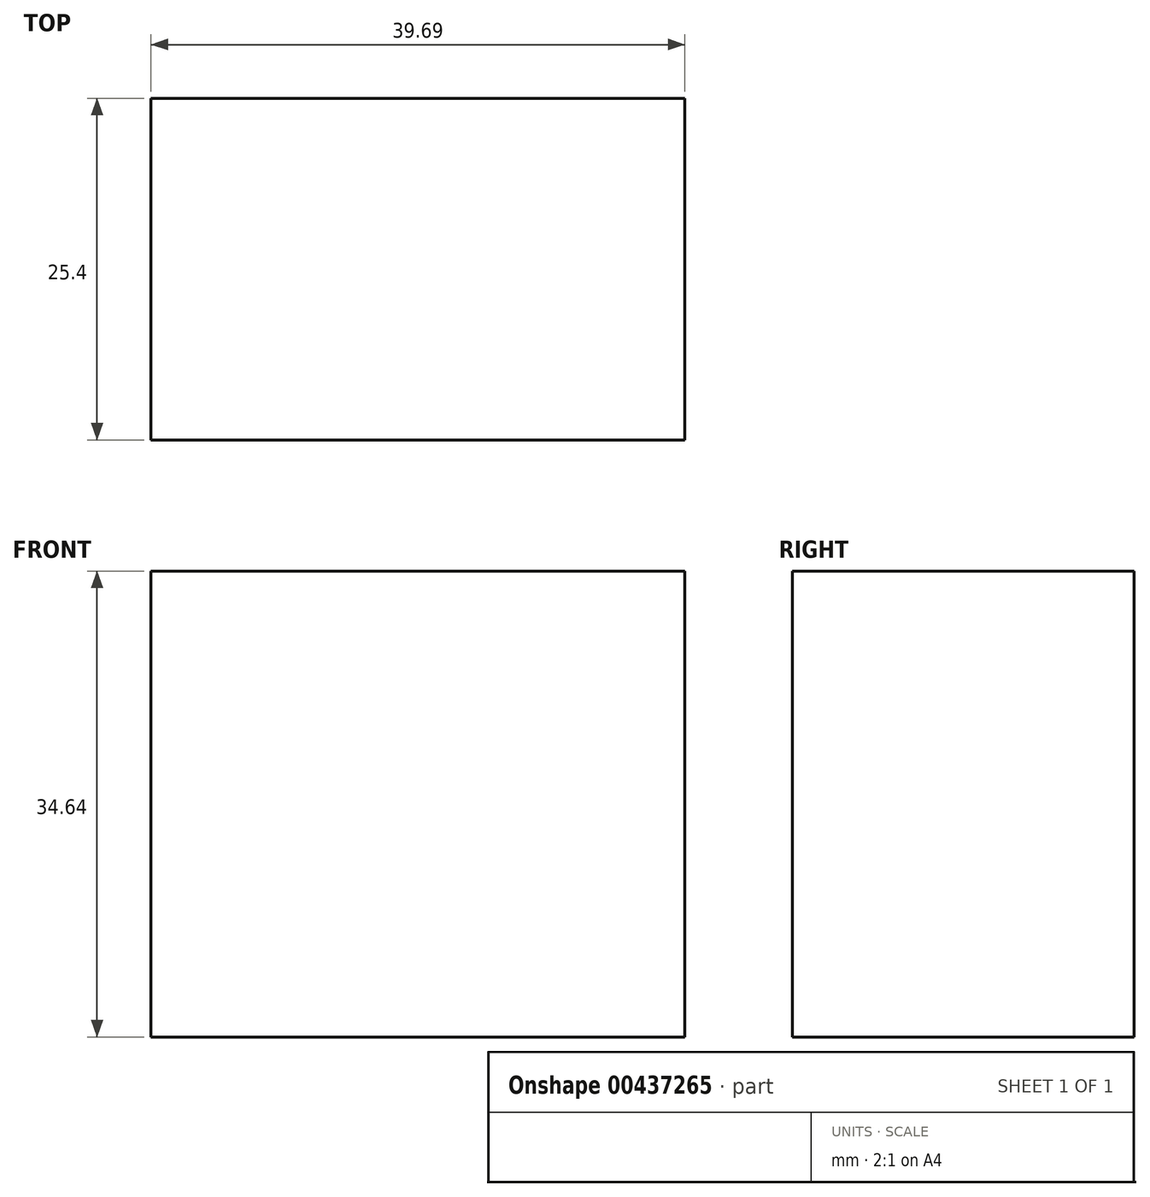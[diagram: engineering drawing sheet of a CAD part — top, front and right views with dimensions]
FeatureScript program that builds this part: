
annotation { "Feature Type Name" : "Feature", "Feature Type Description" : "" }
export const myFeature = defineFeature(function(context is Context, id is Id, definition is map)
    precondition{}
    {
        {
            var Q0;
            Q0=qCreatedBy(makeId("Front.planeOp"),FACE);
            var sketch = newSketch(context, id + "F0", { "sketchPlane" : qUnion([Q0])});
            skLineSegment(sketch, "E0.bottom", {"start": v(-19.7, 19.05) * mm, "end": v(19.99, 19.05) * mm});
            skLineSegment(sketch, "E0.top", {"start": v(-19.7, -15.6) * mm, "end": v(19.99, -15.6) * mm});
            skLineSegment(sketch, "E0.left", {"start": v(-19.7, 19.05) * mm, "end": v(-19.7, -15.6) * mm});
            skLineSegment(sketch, "E0.right", {"start": v(19.99, 19.05) * mm, "end": v(19.99, -15.6) * mm});
            skSolve(sketch);
        }
        {
            var Q0;
            Q0=sQuery(id+"F0.wireOp",EDGE,"E0.left");
            var Q1;
            Q1=sQuery(id+"F0.wireOp",EDGE,"E0.bottom");
            var Q2;
            Q2=sQuery(id+"F0.wireOp",EDGE,"E0.top");
            var Q3;
            Q3=sQuery(id+"F0.wireOp",EDGE,"E0.right");
            extrude(context, id + "F1", {"bodyType" : ToolBodyType.SURFACE, "surfaceEntities" : qUnion([Q0, Q1, Q2, Q3]), "depth" : 25.4 * mm});
        }
    });
